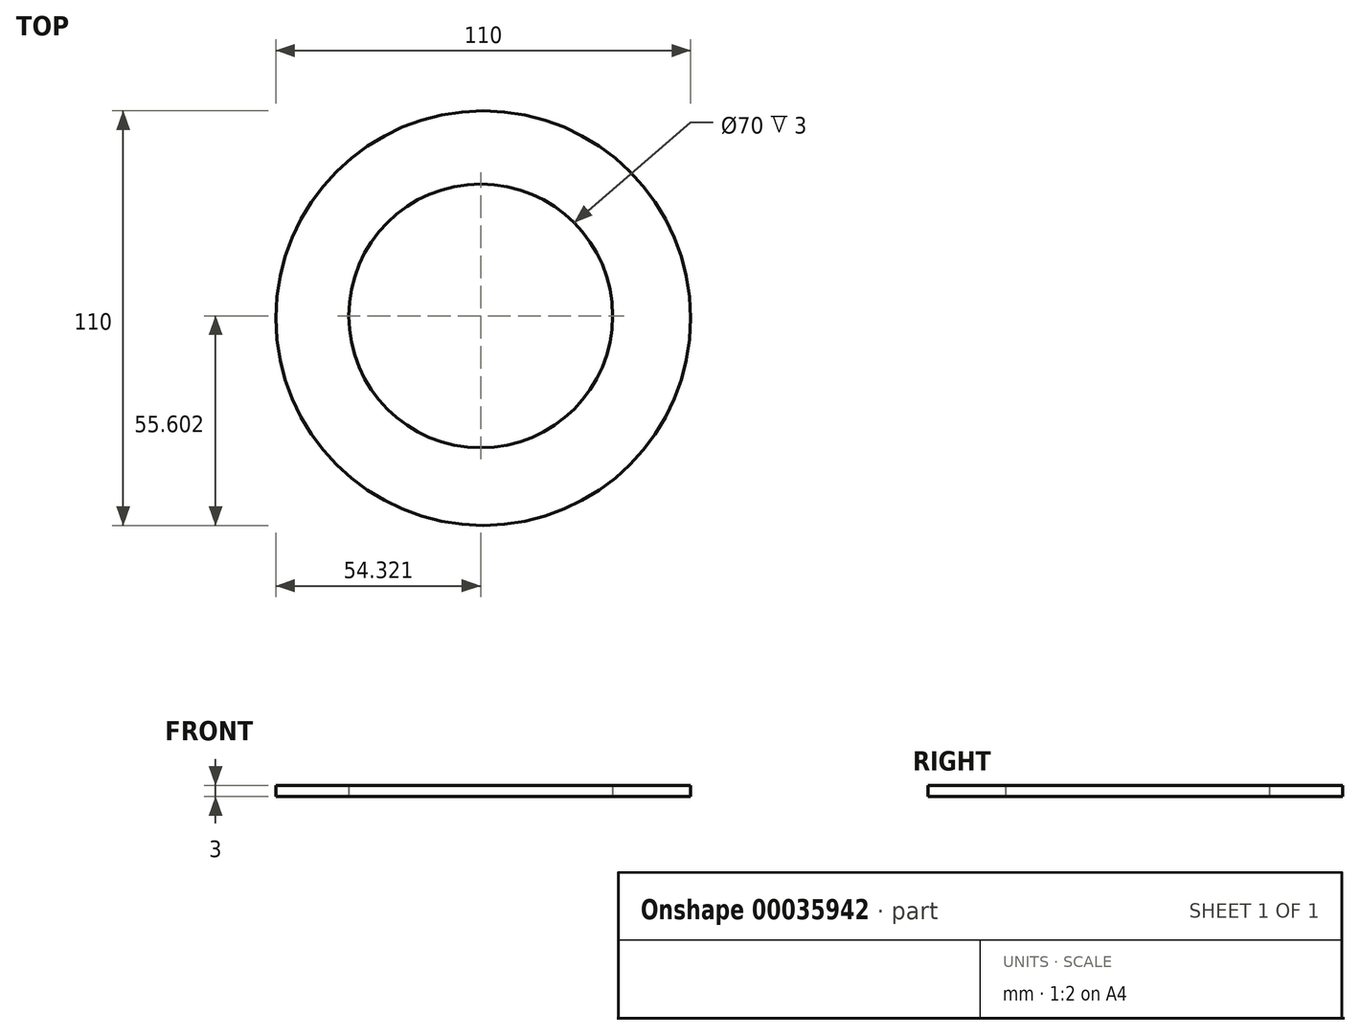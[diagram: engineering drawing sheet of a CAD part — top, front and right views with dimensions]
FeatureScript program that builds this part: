
annotation { "Feature Type Name" : "Feature", "Feature Type Description" : "" }
export const myFeature = defineFeature(function(context is Context, id is Id, definition is map)
    precondition{}
    {
        {
            var Q0;
            Q0=qCreatedBy(makeId("Top.planeOp"),FACE);
            var sketch = newSketch(context, id + "F0", { "sketchPlane" : qUnion([Q0])});
            skCircle(sketch, "E0", {"center": v(-0.68, 0.6) * mm, "radius": 35 * mm});
            skCircle(sketch, "E1", {"center": v(0, 0) * mm, "radius": 55 * mm});
            skSolve(sketch);
        }
        {
            var Q0;
            Q0 = qSketchRegion(id + "F0", true);
            extrude(context, id + "F1", {"entities" : qUnion([Q0]), "depth" : 3 * mm});
        }
    });
